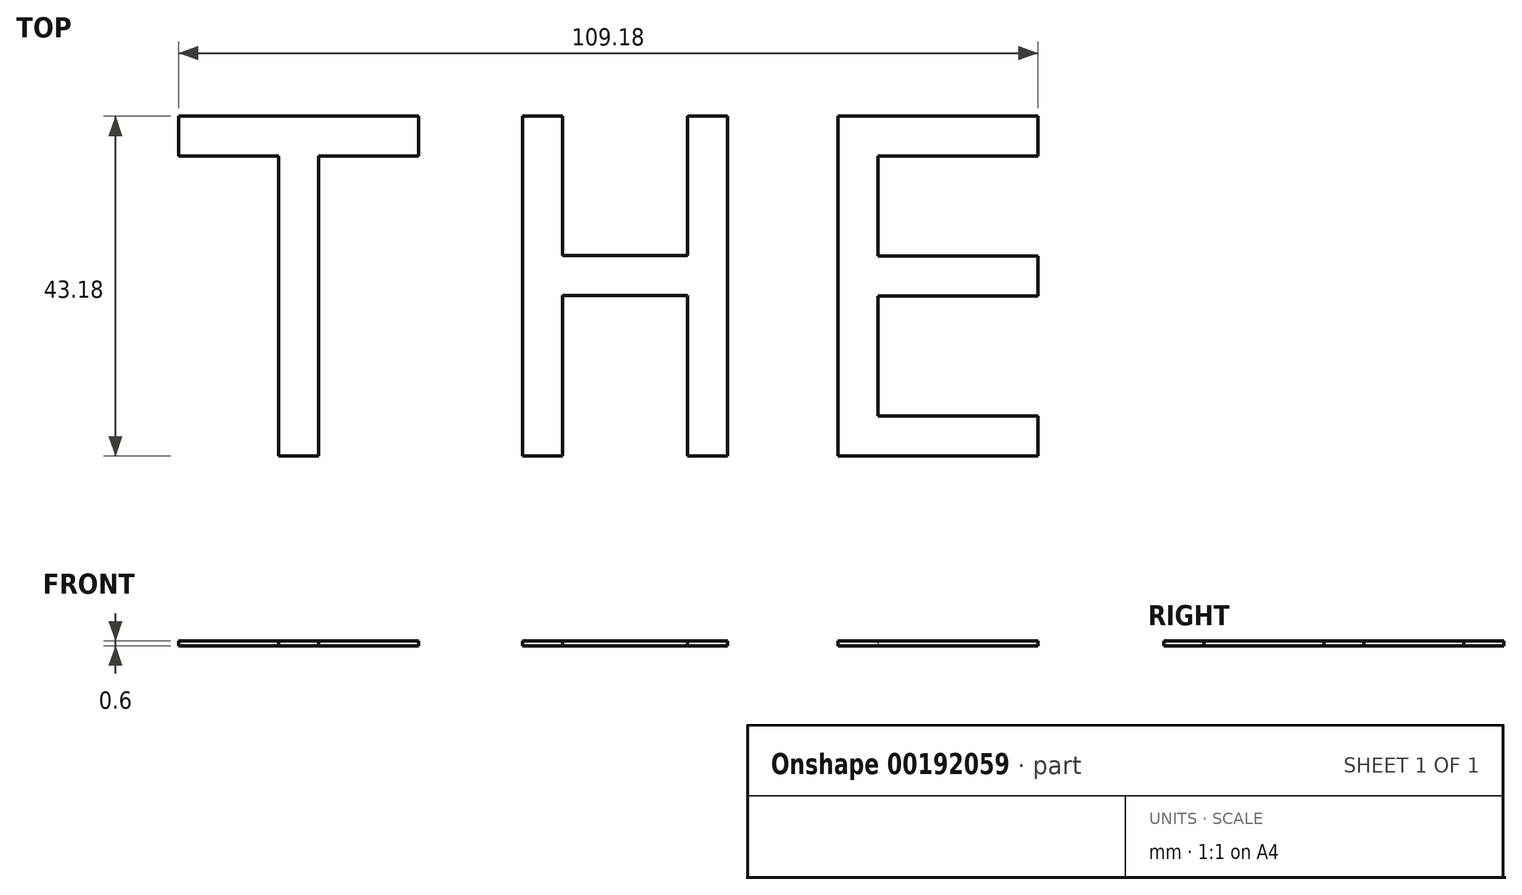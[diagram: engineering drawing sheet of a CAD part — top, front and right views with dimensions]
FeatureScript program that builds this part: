
annotation { "Feature Type Name" : "Feature", "Feature Type Description" : "" }
export const myFeature = defineFeature(function(context is Context, id is Id, definition is map)
    precondition{}
    {
        {
            var Q0;
            Q0=qCreatedBy(makeId("Top.planeOp"),FACE);
            var sketch = newSketch(context, id + "F0", { "sketchPlane" : qUnion([Q0])});
            skLineSegment(sketch, "E0", {"start": v(0, 0) * mm, "end": v(0, 38.1) * mm});
            skLineSegment(sketch, "E1", {"start": v(0, 38.1) * mm, "end": v(-12.7, 38.1) * mm});
            skLineSegment(sketch, "E2", {"start": v(-12.7, 38.1) * mm, "end": v(-12.7, 43.18) * mm});
            skLineSegment(sketch, "E3", {"start": v(-12.7, 43.18) * mm, "end": v(17.78, 43.18) * mm});
            skLineSegment(sketch, "E4", {"start": v(17.78, 43.18) * mm, "end": v(17.78, 38.1) * mm});
            skLineSegment(sketch, "E5", {"start": v(17.78, 38.1) * mm, "end": v(5.08, 38.1) * mm});
            skLineSegment(sketch, "E6", {"start": v(5.08, 38.1) * mm, "end": v(5.08, 0) * mm});
            skLineSegment(sketch, "E7", {"start": v(5.08, 0) * mm, "end": v(0, 0) * mm});
            skLineSegment(sketch, "E8", {"start": v(31, 43.18) * mm, "end": v(31, 0) * mm});
            skLineSegment(sketch, "E9", {"start": v(31, 0) * mm, "end": v(36.08, 0) * mm});
            skLineSegment(sketch, "E10", {"start": v(52, 20.42) * mm, "end": v(52, 0) * mm});
            skLineSegment(sketch, "E11", {"start": v(52, 0) * mm, "end": v(57.07, 0) * mm});
            skLineSegment(sketch, "E12", {"start": v(57.07, 0) * mm, "end": v(57.07, 20.42) * mm});
            skLineSegment(sketch, "E13", {"start": v(36.08, 43.18) * mm, "end": v(31, 43.18) * mm});
            skLineSegment(sketch, "E14", {"start": v(71.08, 43.18) * mm, "end": v(71.08, 0) * mm});
            skLineSegment(sketch, "E15", {"start": v(71.08, 0) * mm, "end": v(96.48, 0) * mm});
            skLineSegment(sketch, "E16", {"start": v(96.48, 0) * mm, "end": v(96.48, 5.08) * mm});
            skLineSegment(sketch, "E17", {"start": v(96.48, 5.08) * mm, "end": v(76.16, 5.08) * mm});
            skLineSegment(sketch, "E18", {"start": v(76.16, 5.08) * mm, "end": v(76.16, 20.32) * mm});
            skLineSegment(sketch, "E19", {"start": v(76.16, 20.32) * mm, "end": v(96.48, 20.32) * mm});
            skLineSegment(sketch, "E20", {"start": v(96.48, 20.32) * mm, "end": v(96.48, 25.4) * mm});
            skLineSegment(sketch, "E21", {"start": v(96.48, 25.4) * mm, "end": v(76.16, 25.4) * mm});
            skLineSegment(sketch, "E22", {"start": v(76.16, 25.4) * mm, "end": v(76.16, 38.1) * mm});
            skLineSegment(sketch, "E23", {"start": v(76.16, 38.1) * mm, "end": v(96.48, 38.1) * mm});
            skLineSegment(sketch, "E24", {"start": v(96.48, 38.1) * mm, "end": v(96.48, 43.18) * mm});
            skLineSegment(sketch, "E25", {"start": v(96.48, 43.18) * mm, "end": v(71.08, 43.18) * mm});
            skLineSegment(sketch, "E26", {"start": v(36.08, 43.18) * mm, "end": v(36.08, 25.5) * mm});
            skLineSegment(sketch, "E27", {"start": v(36.08, 25.5) * mm, "end": v(52, 25.5) * mm});
            skLineSegment(sketch, "E28", {"start": v(52, 25.5) * mm, "end": v(52, 43.18) * mm});
            skLineSegment(sketch, "E29", {"start": v(52, 43.18) * mm, "end": v(57.07, 43.18) * mm});
            skLineSegment(sketch, "E30", {"start": v(57.07, 43.18) * mm, "end": v(57.07, 20.42) * mm});
            skLineSegment(sketch, "E31", {"start": v(52, 20.42) * mm, "end": v(36.08, 20.42) * mm});
            skLineSegment(sketch, "E32", {"start": v(36.08, 20.42) * mm, "end": v(36.08, 0) * mm});
            skSolve(sketch);
        }
        {
            var Q0;
            Q0=makeQuery(id+"F0.imprint","IMPRINT",FACE,{"disambiguationData":[TD([[makeQuery(id+"F0.imprint","IMPRINT",EDGE,{"derivedFrom":sQuery(id+"F0.wireOp",EDGE,"E0")}),-1.0]])]});
            var Q1;
            Q1=makeQuery(id+"F0.imprint","IMPRINT",FACE,{"disambiguationData":[TD([[makeQuery(id+"F0.imprint","IMPRINT",EDGE,{"derivedFrom":sQuery(id+"F0.wireOp",EDGE,"E8")}),1.0]])]});
            var Q2;
            Q2=makeQuery(id+"F0.imprint","IMPRINT",FACE,{"disambiguationData":[TD([[makeQuery(id+"F0.imprint","IMPRINT",EDGE,{"derivedFrom":sQuery(id+"F0.wireOp",EDGE,"E14")}),1.0]])]});
            extrude(context, id + "F1", {"entities" : qUnion([Q0, Q1, Q2]), "depth" : .6 * mm});
        }
    });
